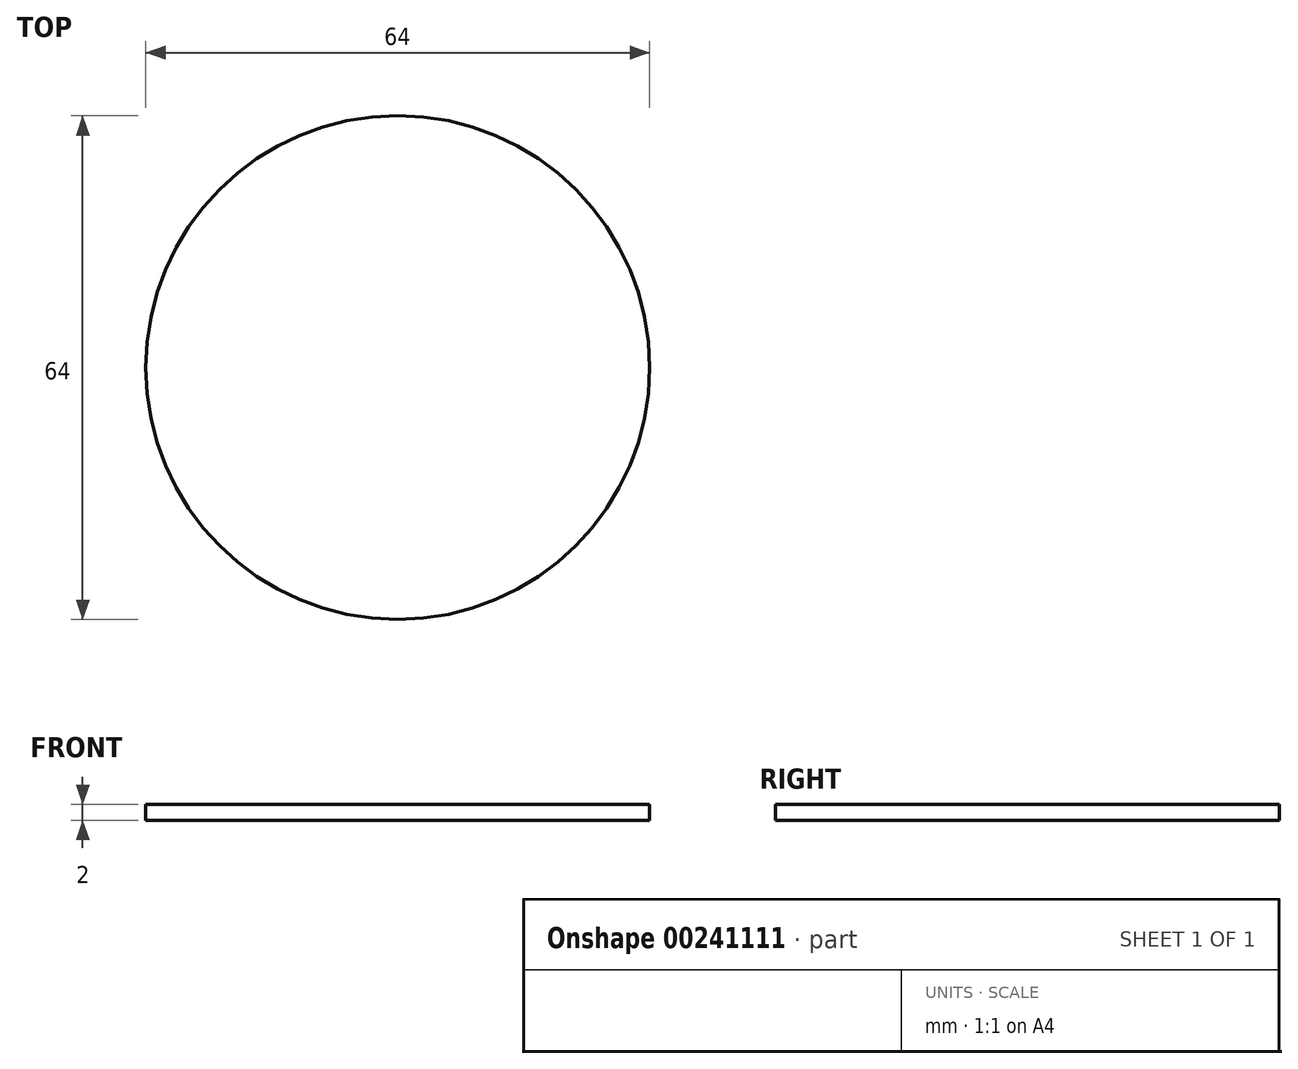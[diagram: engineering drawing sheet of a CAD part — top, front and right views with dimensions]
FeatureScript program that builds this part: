
annotation { "Feature Type Name" : "Feature", "Feature Type Description" : "" }
export const myFeature = defineFeature(function(context is Context, id is Id, definition is map)
    precondition{}
    {
        {
            var Q0;
            Q0=qCreatedBy(makeId("Top.planeOp"),FACE);
            var sketch = newSketch(context, id + "F0", { "sketchPlane" : qUnion([Q0])});
            skCircle(sketch, "E0", {"center": v(0, 0) * mm, "radius": 32 * mm});
            skSolve(sketch);
        }
        {
            var Q0;
            Q0 = qSketchRegion(id + "F0", true);
            extrude(context, id + "F1", {"entities" : qUnion([Q0]), "depth" : 2 * mm});
        }
    });
